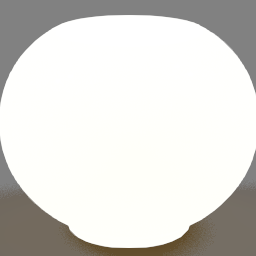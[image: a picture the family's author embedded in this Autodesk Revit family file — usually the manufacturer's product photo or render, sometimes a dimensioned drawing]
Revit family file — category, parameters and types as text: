
# Revit family: 3-040X-xx Compact Mirror
name_source: partatom
category: Lighting Fixtures
units: mm (PartAtom-declared; Revit-internal decimal feet)

## family parameters
Always vertical = Yes
Cut with Voids When Loaded = No
Host = Wall
Light Source = No
OmniClass Number = 23.80.70.00
OmniClass Title = Lighting
Part Type = Normal
Room Calculation Point = No
Round Connector Dimension = Use Diameter
Shared = No

## types (5) — shared parameters
Diffuser = Ghost Mirror
Lamp = LED Array
Manufacturer = Vanita by Oxygen
Metal Finish 1 = 15 - Black
Model = 3-030X-xx / Skylight
References = Ref. 3 = 120 V / Ref. 37 = 277 V
URL = www.oxygenlighting.com
Voltage = 120 V
Voltage Input = 120 V or 277 V - 50/60 Hz
zero-valued in all types: Default Elevation

## per-type parameters (varying)
| type | Height | Wattage Comments | Width |
| 3-0301-15 / Black | 610 mm  [stored 2.00131 ft] | 1 x 83.5 W at 120 V | 914 mm  [stored 2.99869 ft] |
| 3-0302-15 / Black | 914 mm  [stored 2.99869 ft] | 1 x 99.7 W at 120 V | 914 mm  [stored 2.99869 ft] |
| 3-0303-15 / Black | 914 mm  [stored 2.99869 ft] | 1 x 122.6 W at 120 V | 1219 mm |
| 3-0304-15 / Black | 1219 mm | 1 x 167.9 W at 120 V | 1219 mm |
| 3-0305-15 / Black | 1067 mm  [stored 3.50066 ft] | 1 x 167.9 W at 120 V | 1524 mm  [stored 5 ft] |

note: [stored X ft] marks values corroborated as IEEE doubles in the binary element streams (Revit-internal decimal feet)

## geometry (parser evidence)
native form markers: Sweep x5
no freeform markers — native parametric forms only
